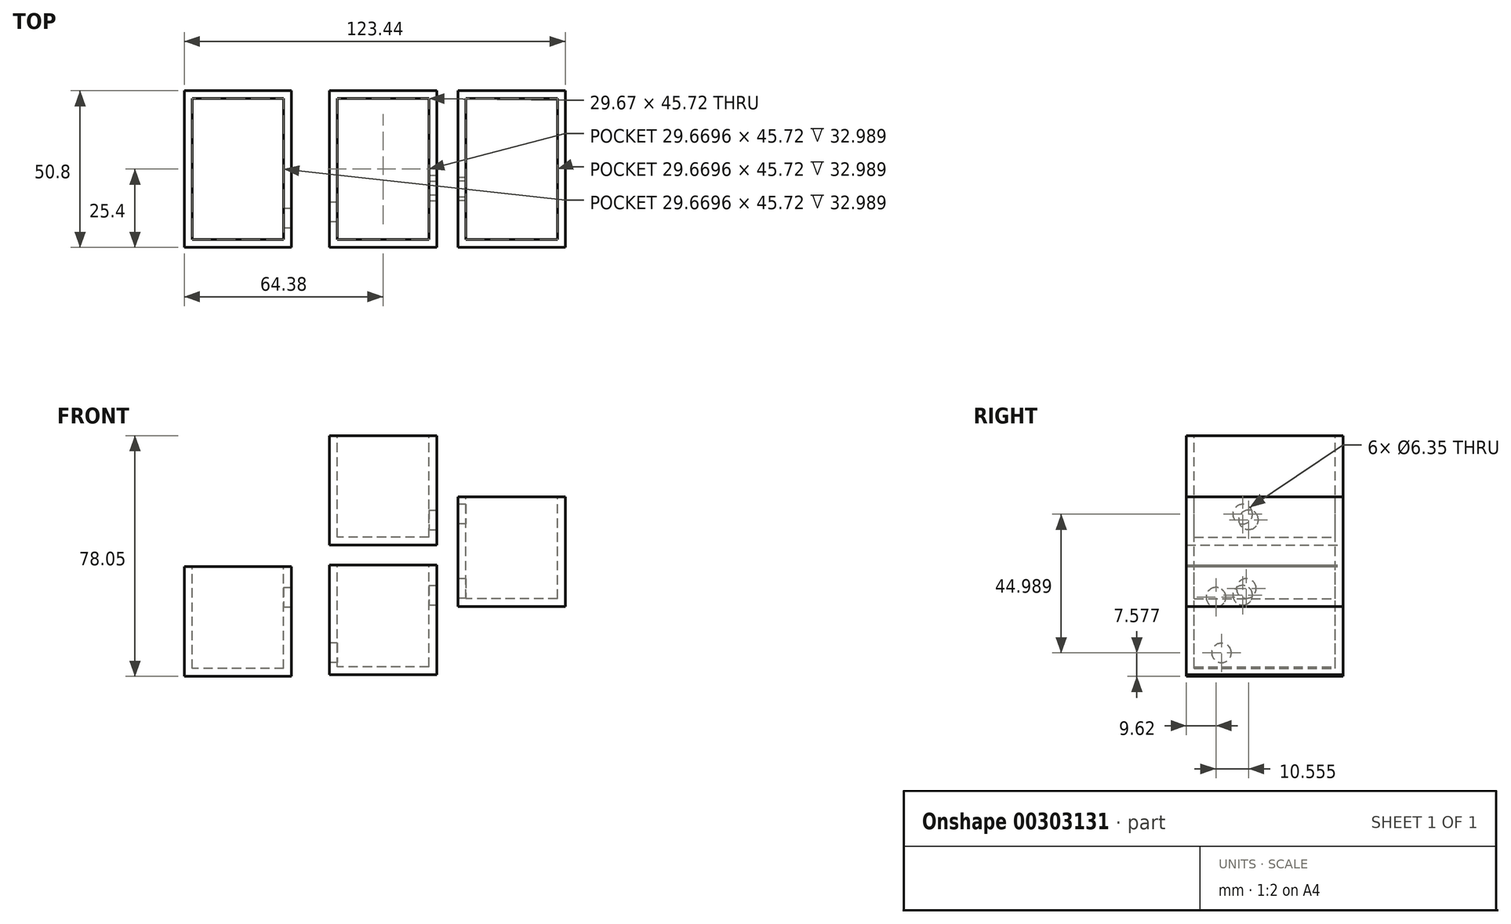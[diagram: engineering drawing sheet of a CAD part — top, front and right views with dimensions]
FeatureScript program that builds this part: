
annotation { "Feature Type Name" : "Feature", "Feature Type Description" : "" }
export const myFeature = defineFeature(function(context is Context, id is Id, definition is map)
    precondition{}
    {
        {
            var Q0;
            Q0=qCreatedBy(makeId("Front.planeOp"),FACE);
            var sketch = newSketch(context, id + "F0", { "sketchPlane" : qUnion([Q0])});
            skLineSegment(sketch, "E0.bottom", {"start": v(17.37, 9.65) * mm, "end": v(-17.37, 9.65) * mm});
            skLineSegment(sketch, "E0.top", {"start": v(17.37, 45.18) * mm, "end": v(-17.37, 45.18) * mm});
            skLineSegment(sketch, "E0.left", {"start": v(17.37, 9.65) * mm, "end": v(17.37, 45.18) * mm});
            skLineSegment(sketch, "E0.right", {"start": v(-17.37, 9.65) * mm, "end": v(-17.37, 45.18) * mm});
            skPoint(sketch, "E0.middle", {"position": v(0, 27.42) * mm});
            skSolve(sketch);
        }
        {
            var Q0;
            Q0=qCreatedBy(makeId("Front.planeOp"),FACE);
            var sketch = newSketch(context, id + "F1", { "sketchPlane" : qUnion([Q0])});
            skLineSegment(sketch, "E1.bottom", {"start": v(59.06, -10.21) * mm, "end": v(24.3, -10.21) * mm});
            skLineSegment(sketch, "E1.top", {"start": v(59.06, 25.32) * mm, "end": v(24.3, 25.32) * mm});
            skLineSegment(sketch, "E1.left", {"start": v(59.06, -10.21) * mm, "end": v(59.06, 25.32) * mm});
            skLineSegment(sketch, "E1.right", {"start": v(24.3, -10.21) * mm, "end": v(24.3, 25.32) * mm});
            skPoint(sketch, "E1.middle", {"position": v(41.68, 7.55) * mm});
            skSolve(sketch);
        }
        {
            var Q0;
            Q0=qCreatedBy(makeId("Front.planeOp"),FACE);
            var sketch = newSketch(context, id + "F2", { "sketchPlane" : qUnion([Q0])});
            skLineSegment(sketch, "E2.bottom", {"start": v(17.37, -32.31) * mm, "end": v(-17.37, -32.31) * mm});
            skLineSegment(sketch, "E2.top", {"start": v(17.37, 3.22) * mm, "end": v(-17.37, 3.22) * mm});
            skLineSegment(sketch, "E2.left", {"start": v(17.37, -32.31) * mm, "end": v(17.37, 3.22) * mm});
            skLineSegment(sketch, "E2.right", {"start": v(-17.37, -32.31) * mm, "end": v(-17.37, 3.22) * mm});
            skPoint(sketch, "E2.middle", {"position": v(0, -14.55) * mm});
            skSolve(sketch);
        }
        {
            var Q0;
            Q0=qCreatedBy(makeId("Front.planeOp"),FACE);
            var sketch = newSketch(context, id + "F3", { "sketchPlane" : qUnion([Q0])});
            skLineSegment(sketch, "E3.bottom", {"start": v(-29.63, -32.87) * mm, "end": v(-64.38, -32.87) * mm});
            skLineSegment(sketch, "E3.top", {"start": v(-29.63, 2.66) * mm, "end": v(-64.38, 2.66) * mm});
            skLineSegment(sketch, "E3.left", {"start": v(-29.63, -32.87) * mm, "end": v(-29.63, 2.66) * mm});
            skLineSegment(sketch, "E3.right", {"start": v(-64.38, -32.87) * mm, "end": v(-64.38, 2.66) * mm});
            skPoint(sketch, "E3.middle", {"position": v(-47, -15.1) * mm});
            skSolve(sketch);
        }
        {
            var Q0;
            Q0=makeQuery(id+"F0.imprint","IMPRINT",FACE,{"disambiguationData":[TD([[makeQuery(id+"F0.imprint","IMPRINT",EDGE,{"derivedFrom":sQuery(id+"F0.wireOp",EDGE,"E0.bottom")}),-1.0]])]});
            var Q1;
            Q1=makeQuery(id+"F1.imprint","IMPRINT",FACE,{"disambiguationData":[TD([[makeQuery(id+"F1.imprint","IMPRINT",EDGE,{"derivedFrom":sQuery(id+"F1.wireOp",EDGE,"E1.bottom")}),-1.0]])]});
            var Q2;
            Q2=makeQuery(id+"F2.imprint","IMPRINT",FACE,{"disambiguationData":[TD([[makeQuery(id+"F2.imprint","IMPRINT",EDGE,{"derivedFrom":sQuery(id+"F2.wireOp",EDGE,"E2.bottom")}),-1.0]])]});
            var Q3;
            Q3=makeQuery(id+"F3.imprint","IMPRINT",FACE,{"disambiguationData":[TD([[makeQuery(id+"F3.imprint","IMPRINT",EDGE,{"derivedFrom":sQuery(id+"F3.wireOp",EDGE,"E3.bottom")}),-1.0]])]});
            extrude(context, id + "F4", {"entities" : qUnion([Q0, Q1, Q2, Q3]), "depth" : 50.8 * mm});
        }
        {
            var Q0;
            Q0=makeQuery(id+"F4.opExtrude","SWEPT_FACE",FACE,{"disambiguationData":[OSD([sQuery(id+"F3.wireOp",EDGE,"E3.top")])]});
            var Q1;
            Q1=makeQuery(id+"F4.opExtrude","SWEPT_FACE",FACE,{"disambiguationData":[OSD([sQuery(id+"F2.wireOp",EDGE,"E2.top")])]});
            var Q2;
            Q2=makeQuery(id+"F4.opExtrude","SWEPT_FACE",FACE,{"disambiguationData":[OSD([sQuery(id+"F0.wireOp",EDGE,"E0.top")])]});
            var Q3;
            Q3=makeQuery(id+"F4.opExtrude","SWEPT_FACE",FACE,{"disambiguationData":[OSD([sQuery(id+"F1.wireOp",EDGE,"E1.top")])]});
            shell(context, id + "F5", {"entities" : qUnion([Q0, Q1, Q2, Q3]), "thickness" : 2.54 * mm});
        }
        {
            var Q0;
            Q0=makeQuery(id+"F4.opExtrude","SWEPT_FACE",FACE,{"disambiguationData":[OSD([sQuery(id+"F0.wireOp",EDGE,"E0.left")])]});
            var sketch = newSketch(context, id + "F6", { "sketchPlane" : qUnion([Q0])});
            skCircle(sketch, "E4", {"center": v(-30.63, 17.87) * mm, "radius": 2.37 * mm});
            skSolve(sketch);
        }
        {
            var Q0;
            Q0=sQuery(id+"F6.wireOp",VERTEX,"E4.center");
            var Q1;
            Q1=makeQuery(id+"F4.opExtrude","SWEPT_BODY",BODY,{"disambiguationData":[OSD([sQuery(id+"F0.wireOp",EDGE,"E0.bottom"),sQuery(id+"F0.wireOp",EDGE,"E0.top"),sQuery(id+"F0.wireOp",EDGE,"E0.left"),sQuery(id+"F0.wireOp",EDGE,"E0.right")])]});
            hole(context, id + "F7", {"style" : HoleStyle.SIMPLE, "endStyle" : HoleEndStyle.BLIND, "holeDiameter" : 6.35 * mm, "holeDepth" : 12.7 * mm, "tappedDepth" : 12.7 * mm, "tapClearance" : 3, "locations" : qUnion([Q0]), "scope" : qUnion([Q1])});
        }
        {
            var Q0;
            Q0=makeQuery(id+"F4.opExtrude","SWEPT_FACE",FACE,{"disambiguationData":[OSD([sQuery(id+"F1.wireOp",EDGE,"E1.right")])]});
            var sketch = newSketch(context, id + "F8", { "sketchPlane" : qUnion([Q0])});
            skCircle(sketch, "E5", {"center": v(32.52, 19.7) * mm, "radius": 2.37 * mm});
            skSolve(sketch);
        }
        {
            var Q0;
            Q0=sQuery(id+"F8.wireOp",VERTEX,"E5.center");
            var Q1;
            Q1=makeQuery(id+"F4.opExtrude","SWEPT_BODY",BODY,{"disambiguationData":[OSD([sQuery(id+"F1.wireOp",EDGE,"E1.bottom"),sQuery(id+"F1.wireOp",EDGE,"E1.top"),sQuery(id+"F1.wireOp",EDGE,"E1.left"),sQuery(id+"F1.wireOp",EDGE,"E1.right")])]});
            hole(context, id + "F9", {"style" : HoleStyle.SIMPLE, "endStyle" : HoleEndStyle.BLIND, "holeDiameter" : 6.35 * mm, "holeDepth" : 12.7 * mm, "tappedDepth" : 12.7 * mm, "tapClearance" : 3, "locations" : qUnion([Q0]), "scope" : qUnion([Q1])});
        }
        {
            var Q0;
            Q0=makeQuery(id+"F4.opExtrude","SWEPT_FACE",FACE,{"disambiguationData":[OSD([sQuery(id+"F1.wireOp",EDGE,"E1.right")])]});
            var sketch = newSketch(context, id + "F10", { "sketchPlane" : qUnion([Q0])});
            skCircle(sketch, "E6", {"center": v(31.35, -4.4) * mm, "radius": 2.37 * mm});
            skSolve(sketch);
        }
        {
            var Q0;
            Q0=sQuery(id+"F10.wireOp",VERTEX,"E6.center");
            var Q1;
            Q1=makeQuery(id+"F4.opExtrude","SWEPT_BODY",BODY,{"disambiguationData":[OSD([sQuery(id+"F1.wireOp",EDGE,"E1.bottom"),sQuery(id+"F1.wireOp",EDGE,"E1.top"),sQuery(id+"F1.wireOp",EDGE,"E1.left"),sQuery(id+"F1.wireOp",EDGE,"E1.right")])]});
            hole(context, id + "F11", {"style" : HoleStyle.SIMPLE, "endStyle" : HoleEndStyle.BLIND, "holeDiameter" : 6.35 * mm, "holeDepth" : 12.7 * mm, "tappedDepth" : 12.7 * mm, "tapClearance" : 3, "locations" : qUnion([Q0]), "scope" : qUnion([Q1])});
        }
        {
            var Q0;
            Q0=makeQuery(id+"F4.opExtrude","SWEPT_FACE",FACE,{"disambiguationData":[OSD([sQuery(id+"F2.wireOp",EDGE,"E2.left")])]});
            var sketch = newSketch(context, id + "F12", { "sketchPlane" : qUnion([Q0])});
            skCircle(sketch, "E7", {"center": v(-129.73, 13.88) * mm, "radius": 2.37 * mm});
            skCircle(sketch, "E8", {"center": v(-32.52, -6.59) * mm, "radius": 2.37 * mm});
            skSolve(sketch);
        }
        {
            var Q0;
            Q0=sQuery(id+"F12.wireOp",VERTEX,"E8.center");
            var Q1;
            Q1=makeQuery(id+"F4.opExtrude","SWEPT_BODY",BODY,{"disambiguationData":[OSD([sQuery(id+"F2.wireOp",EDGE,"E2.bottom"),sQuery(id+"F2.wireOp",EDGE,"E2.top"),sQuery(id+"F2.wireOp",EDGE,"E2.left"),sQuery(id+"F2.wireOp",EDGE,"E2.right")])]});
            hole(context, id + "F13", {"style" : HoleStyle.SIMPLE, "endStyle" : HoleEndStyle.BLIND, "holeDiameter" : 6.35 * mm, "holeDepth" : 12.7 * mm, "tappedDepth" : 12.7 * mm, "tapClearance" : 3, "locations" : qUnion([Q0]), "scope" : qUnion([Q1])});
        }
        {
            var Q0;
            Q0=makeQuery(id+"F4.opExtrude","SWEPT_FACE",FACE,{"disambiguationData":[OSD([sQuery(id+"F2.wireOp",EDGE,"E2.right")])]});
            var sketch = newSketch(context, id + "F14", { "sketchPlane" : qUnion([Q0])});
            skCircle(sketch, "E9", {"center": v(39.37, -25.3) * mm, "radius": 2.37 * mm});
            skSolve(sketch);
        }
        {
            var Q0;
            Q0=sQuery(id+"F14.wireOp",VERTEX,"E9.center");
            var Q1;
            Q1=makeQuery(id+"F4.opExtrude","SWEPT_BODY",BODY,{"disambiguationData":[OSD([sQuery(id+"F2.wireOp",EDGE,"E2.bottom"),sQuery(id+"F2.wireOp",EDGE,"E2.top"),sQuery(id+"F2.wireOp",EDGE,"E2.left"),sQuery(id+"F2.wireOp",EDGE,"E2.right")])]});
            hole(context, id + "F15", {"style" : HoleStyle.SIMPLE, "endStyle" : HoleEndStyle.BLIND, "holeDiameter" : 6.35 * mm, "holeDepth" : 12.7 * mm, "tappedDepth" : 12.7 * mm, "tapClearance" : 3, "locations" : qUnion([Q0]), "scope" : qUnion([Q1])});
        }
        {
            var Q0;
            Q0=makeQuery(id+"F4.opExtrude","SWEPT_FACE",FACE,{"disambiguationData":[OSD([sQuery(id+"F3.wireOp",EDGE,"E3.left")])]});
            var sketch = newSketch(context, id + "F16", { "sketchPlane" : qUnion([Q0])});
            skCircle(sketch, "E10", {"center": v(-41.18, -7.22) * mm, "radius": 2.37 * mm});
            skSolve(sketch);
        }
        {
            var Q0;
            Q0=sQuery(id+"F16.wireOp",VERTEX,"E10.center");
            var Q1;
            Q1=makeQuery(id+"F4.opExtrude","SWEPT_BODY",BODY,{"disambiguationData":[OSD([sQuery(id+"F3.wireOp",EDGE,"E3.bottom"),sQuery(id+"F3.wireOp",EDGE,"E3.top"),sQuery(id+"F3.wireOp",EDGE,"E3.left"),sQuery(id+"F3.wireOp",EDGE,"E3.right")])]});
            hole(context, id + "F17", {"style" : HoleStyle.SIMPLE, "endStyle" : HoleEndStyle.BLIND, "holeDiameter" : 6.35 * mm, "holeDepth" : 12.7 * mm, "tappedDepth" : 12.7 * mm, "tapClearance" : 3, "locations" : qUnion([Q0]), "scope" : qUnion([Q1])});
        }
    });
